# Revit family: SURREAL SIDE FIX
name_source: partatom
category: Generic Models
units: mm (PartAtom-declared; Revit-internal decimal feet)

## family parameters
Always vertical = Yes
Can host rebar = No
Cut with Voids When Loaded = No
Part Type = Normal
Room Calculation Point = No
Round Connector Dimension = Use Diameter
Shared = No
Work Plane-Based = No

## types (7) — shared parameters
Keynote = UNEX SYSTEMS, SURREAL SIDE FIX BALUSTRADE
MAX POST SPACING = 1000 mm  [stored 3.28084 ft]
Manufacturer = UNEX SYSTEMS
URL = WWW.UNEX.CO.NZ
zero-valued in all types: Default Elevation

## per-type parameters (varying)
| type | ART TOP RAIL | Description | HAND RAIL HEIGHT | HAND RAIL ON / OFF | HEIGHT | Hand Rail Height | LENGTH | LLR (Round hand rail) | Model | PPR TOP RAIL | Pannel QTY | Post Height | Post QTY | VRE TOP RAIL | VRR TOP RAIL | VRT TOP RAIL |
| SURREAL WITH VRE-SIDE FIX | No | UNEX SURREAL SEMI-FRAMELESS GLASS WITH VRE RAIL | 950 mm  [stored 3.1168 ft] | Yes | 1100 mm | 950 mm  [stored 3.1168 ft] | 2500 mm  [stored 8.2021 ft] | No | UNEX, SURREAL SIDE FIX (VRE) | No | 3 | 1084 mm  [stored 3.55643 ft] | 4 | Yes | No | No |
| SURREAL WITH PRR-SIDE FIX | No | UNEX SURREAL SEMI-FRAMELESS GLASS WITH PRR RAIL | 950 mm  [stored 3.1168 ft] | Yes | 1100 mm | 950 mm  [stored 3.1168 ft] | 3654 mm  [stored 11.9882 ft] | No | UNEX, SURREAL SIDE FIX (PRR) | Yes | 4 | 1084 mm  [stored 3.55643 ft] | 5 | No | No | No |
| SURREAL WITH ART-SIDE FIX | Yes | UNEX SURREAL SEMI-FRAMELESS GLASS WITH ART  RAIL | 950 mm  [stored 3.1168 ft] | Yes | 1100 mm | 950 mm  [stored 3.1168 ft] | 2500 mm  [stored 8.2021 ft] | No | UNEX, SURREAL SIDE FIX (ART) | No | 3 | 1084 mm  [stored 3.55643 ft] | 4 | No | No | No |
| SURREAL WITH VRT-SIDE FIX | No | UNEX SURREAL SEMI-FRAMELESS GLASS WITH VRT RAIL | 950 mm  [stored 3.1168 ft] | Yes | 1100 mm | 950 mm  [stored 3.1168 ft] | 2500 mm  [stored 8.2021 ft] | No | UNEX, SURREAL SIDE FIX (VRT) | No | 3 | 1084 mm  [stored 3.55643 ft] | 4 | No | No | Yes |
| SURREAL WITH VRR-SIDE FIX | No | UNEX SURREAL SEMI-FRAMELESS GLASS WITH VRR RAIL | 950 mm  [stored 3.1168 ft] | Yes | 1100 mm | 950 mm  [stored 3.1168 ft] | 2500 mm  [stored 8.2021 ft] | No | UNEX, SURREAL SIDE FIX (VRR) | No | 3 | 1084 mm  [stored 3.55643 ft] | 4 | No | Yes | No |
| SURREAL WITH LRR-SIDE FIX | No | UNEX SURREAL SEMI-FRAMELESS GLASS WITH LLR RAIL | 1050 mm  [stored 3.44488 ft] | Yes | 1200 mm  [stored 3.93701 ft] | 1050 mm  [stored 3.44488 ft] | 3265 mm  [stored 10.7119 ft] | Yes | UNEX, SURREAL SIDE FIX (LLR) | No | 3 | 1184 mm  [stored 3.88451 ft] | 4 | No | No | No |
| SURREAL (NO RAIL)-SIDE FIX | No | UNEX SURREAL SEMI-FRAMELESS GLASS WITH NO RAIL | 950 mm  [stored 3.1168 ft] | No | 1200 mm  [stored 3.93701 ft] | 950 mm  [stored 3.1168 ft] | 2100 mm | No | UNEX, SURREAL SIDE FIX (NO RAIL) | No | 2 | 1184 mm  [stored 3.88451 ft] | 3 | No | No | No |

note: [stored X ft] marks values corroborated as IEEE doubles in the binary element streams (Revit-internal decimal feet)

## geometry (parser evidence)
native form markers: Blend x4, Sweep x36
no freeform markers — native parametric forms only
